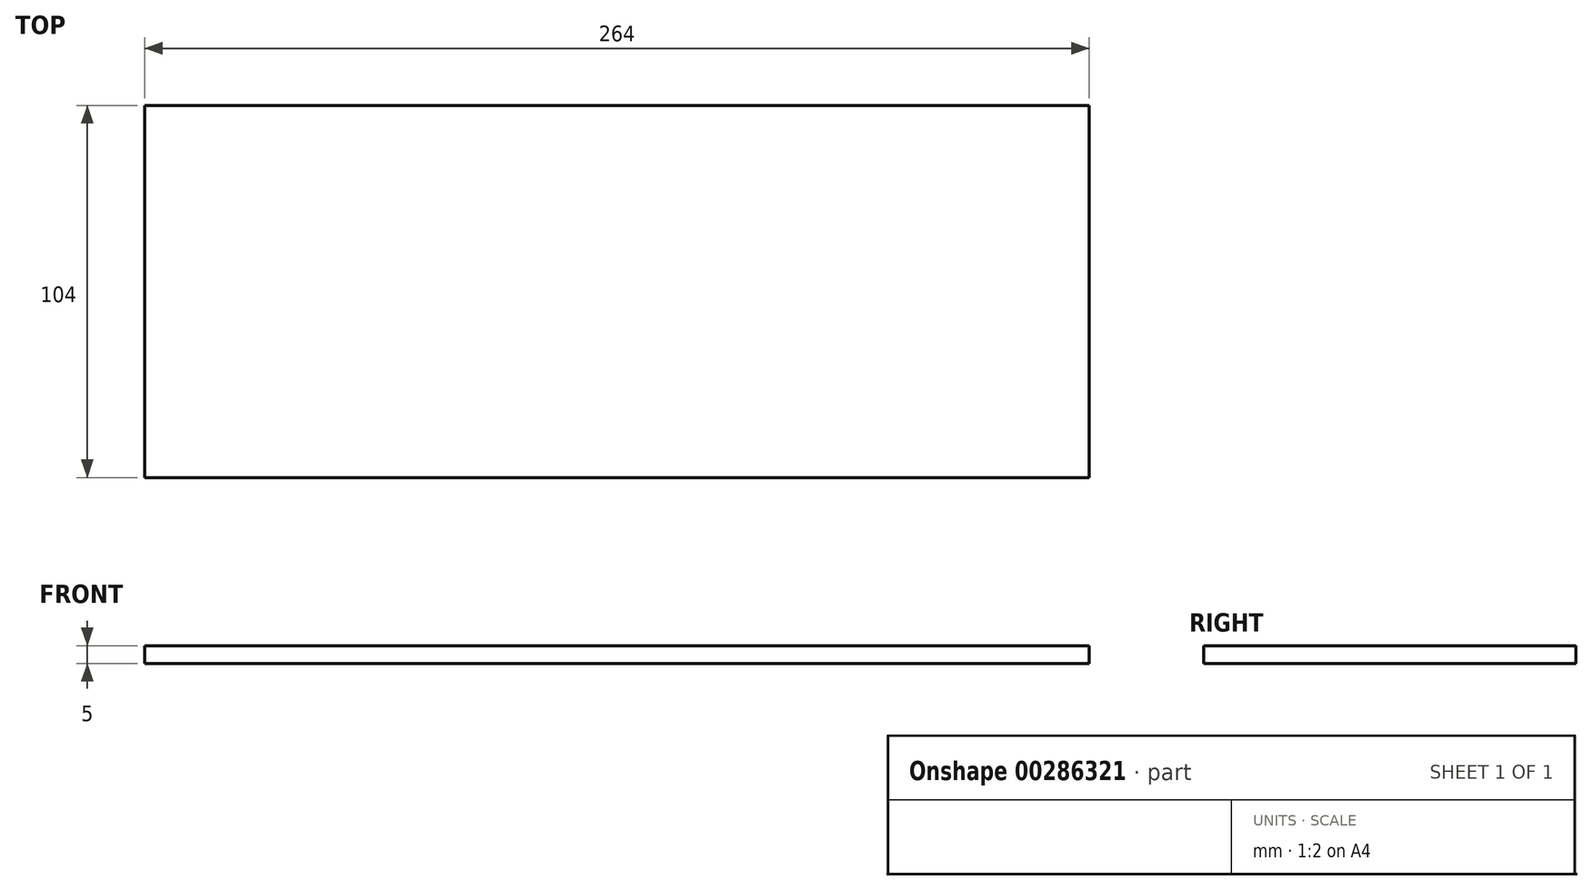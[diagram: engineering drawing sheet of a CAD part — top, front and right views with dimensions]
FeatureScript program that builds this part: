
annotation { "Feature Type Name" : "Feature", "Feature Type Description" : "" }
export const myFeature = defineFeature(function(context is Context, id is Id, definition is map)
    precondition{}
    {
        {
            assignVariable(context, id + "F0", {"name" : "plankX", "anyValue" : 264});
        }
        {
            var Q0;
            Q0=qCreatedBy(makeId("Right.planeOp"),FACE);
            var sketch = newSketch(context, id + "F1", { "sketchPlane" : qUnion([Q0])});
            skLineSegment(sketch, "E0", {"start": v(0, 0) * mm, "end": v(-52, 0) * mm});
            skLineSegment(sketch, "E1", {"start": v(-52, 0) * mm, "end": v(-52, -2.5) * mm});
            skLineSegment(sketch, "E2", {"start": v(-52, -2.5) * mm, "end": v(52, -2.5) * mm});
            skLineSegment(sketch, "E3", {"start": v(52, -2.5) * mm, "end": v(52, 2.5) * mm});
            skLineSegment(sketch, "E4", {"start": v(52, 2.5) * mm, "end": v(-52, 2.5) * mm});
            skLineSegment(sketch, "E5", {"start": v(-52, 2.5) * mm, "end": v(-52, 0) * mm});
            skSolve(sketch);
        }
        {
            var Q0;
            Q0=makeQuery(id+"F1.imprint","IMPRINT",FACE,{"disambiguationData":[TD([[makeQuery(id+"F1.imprint","IMPRINT",EDGE,{"derivedFrom":sQuery(id+"F1.wireOp",EDGE,"E1")}),1.0]])]});
            extrude(context, id + "F2", {"entities" : qUnion([Q0]), "depth" : (getVariable(context, 'plankX') / 2) * mm});
        }
        {
            var Q0;
            Q0=makeQuery(id+"F2.opExtrude","CAP_FACE",FACE,{"disambiguationData":[OSD([sQuery(id+"F1.wireOp",EDGE,"E1"),sQuery(id+"F1.wireOp",EDGE,"E2"),sQuery(id+"F1.wireOp",EDGE,"E3"),sQuery(id+"F1.wireOp",EDGE,"E4"),sQuery(id+"F1.wireOp",EDGE,"E5")])],"isStart":true});
            extrude(context, id + "F3", {"entities" : qUnion([Q0]), "operationType" : NewBodyOperationType.ADD, "depth" : (getVariable(context, 'plankX') / 2) * mm});
        }
    });
